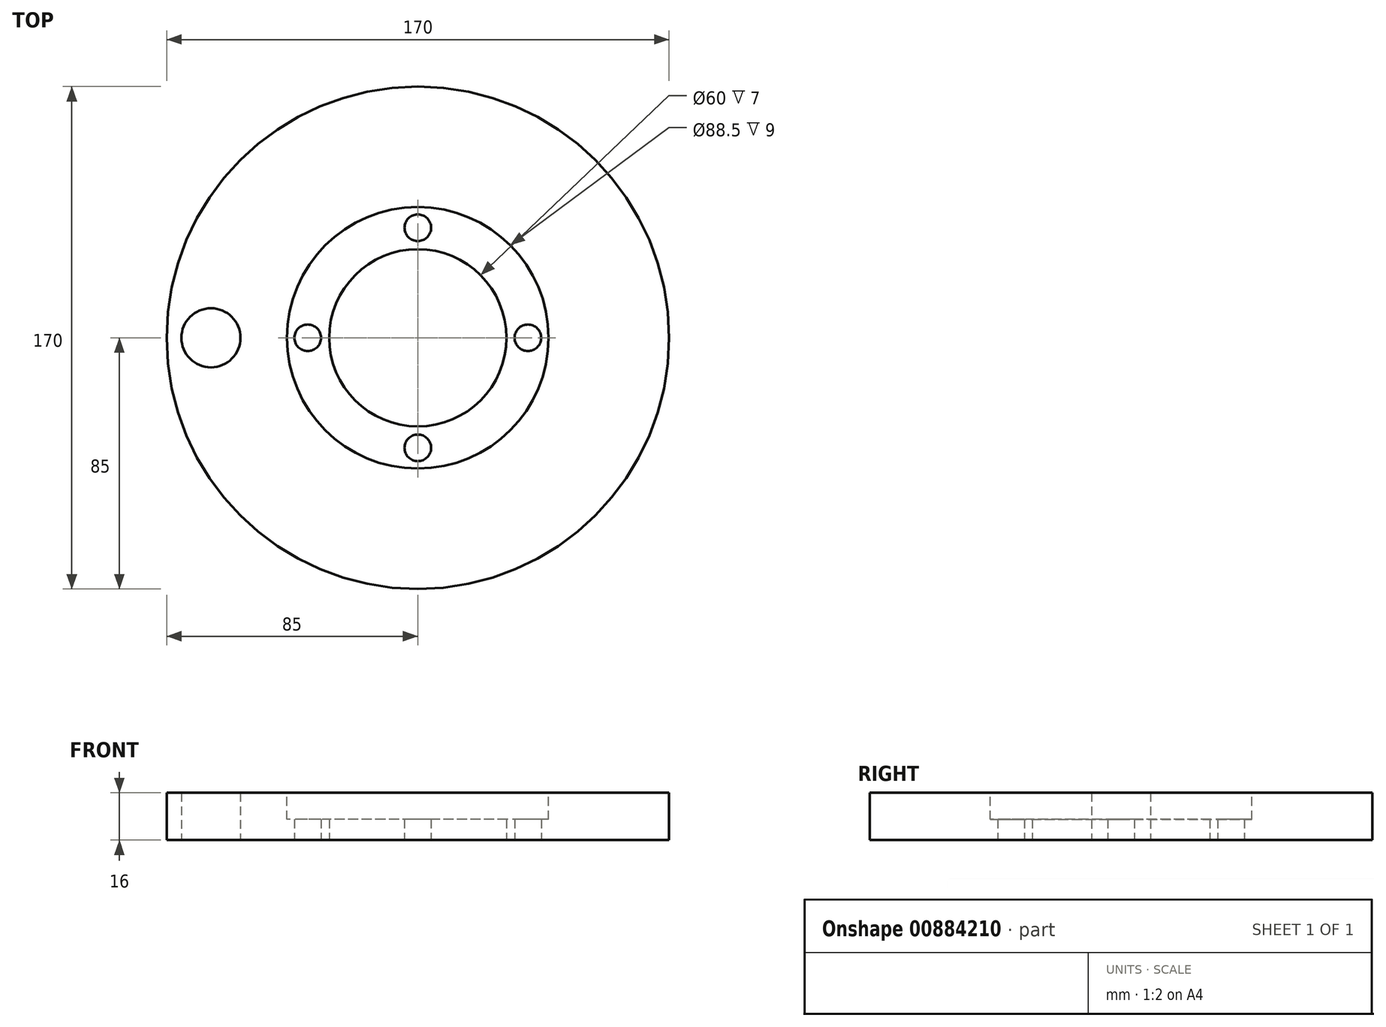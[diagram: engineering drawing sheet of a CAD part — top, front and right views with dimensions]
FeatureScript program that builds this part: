
annotation { "Feature Type Name" : "Feature", "Feature Type Description" : "" }
export const myFeature = defineFeature(function(context is Context, id is Id, definition is map)
    precondition{}
    {
        {
            var Q0;
            Q0=qCreatedBy(makeId("Top.planeOp"),FACE);
            var sketch = newSketch(context, id + "F0", { "sketchPlane" : qUnion([Q0])});
            skCircle(sketch, "E0", {"center": v(0, 0) * mm, "radius": 85 * mm});
            skCircle(sketch, "E1", {"center": v(0, 0) * mm, "radius": 30 * mm});
            skCircle(sketch, "E2", {"center": v(0, 0) * mm, "radius": 37.25 * mm, "construction": true});
            skCircle(sketch, "E3", {"center": v(0, 37.25) * mm, "radius": 4.5 * mm});
            skCircle(sketch, "E4.1.0", {"center": v(-37.25, 0) * mm, "radius": 4.5 * mm});
            skCircle(sketch, "E4.2.0", {"center": v(0, -37.25) * mm, "radius": 4.5 * mm});
            skCircle(sketch, "E4.3.0", {"center": v(37.25, 0) * mm, "radius": 4.5 * mm});
            skCircle(sketch, "E5", {"center": v(-70, 0) * mm, "radius": 10 * mm});
            skSolve(sketch);
        }
        {
            var Q0;
            Q0=makeQuery(id+"F0.imprint","IMPRINT",FACE,{"disambiguationData":[TD([[makeQuery(id+"F0.imprint","IMPRINT",EDGE,{"derivedFrom":sQuery(id+"F0.wireOp",EDGE,"E0")}),1.0]])]});
            extrude(context, id + "F1", {"entities" : qUnion([Q0]), "depth" : 16 * mm, "offsetDistance" : 25 * mm});
        }
        {
            var Q0;
            Q0=makeQuery(id+"F1.opExtrude","CAP_FACE",FACE,{"disambiguationData":[OSD([sQuery(id+"F0.wireOp",EDGE,"E0"),sQuery(id+"F0.wireOp",EDGE,"E1"),sQuery(id+"F0.wireOp",EDGE,"E3"),sQuery(id+"F0.wireOp",EDGE,"E4.1.0"),sQuery(id+"F0.wireOp",EDGE,"E4.2.0"),sQuery(id+"F0.wireOp",EDGE,"E4.3.0"),sQuery(id+"F0.wireOp",EDGE,"E5")])],"isStart":false});
            var sketch = newSketch(context, id + "F2", { "sketchPlane" : qUnion([Q0])});
            skCircle(sketch, "E6", {"center": v(0, 0) * mm, "radius": 44.25 * mm});
            skSolve(sketch);
        }
        {
            var Q0;
            Q0=makeQuery(id+"F2.imprint","IMPRINT",FACE,{"disambiguationData":[TD([[makeQuery(id+"F2.imprint","IMPRINT",EDGE,{"derivedFrom":sQuery(id+"F2.wireOp",EDGE,"E6")}),1.0]])]});
            extrude(context, id + "F3", {"entities" : qUnion([Q0]), "operationType" : NewBodyOperationType.REMOVE, "oppositeDirection" : true, "depth" : 9 * mm, "offsetDistance" : 25 * mm});
        }
    });
